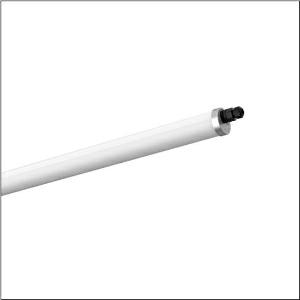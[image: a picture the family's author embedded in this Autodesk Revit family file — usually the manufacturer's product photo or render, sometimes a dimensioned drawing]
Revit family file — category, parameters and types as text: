
# Revit family: monsun_r__31_tube_51ft10dn4a0a_ff33
name_source: partatom
category: Lighting Fixtures
units: mm (PartAtom-declared; Revit-internal decimal feet)

## family parameters
Cut with Voids When Loaded = No
Host = Face
Light Source = No
Part Type = Normal
Room Calculation Point = No
Round Connector Dimension = Use Diameter
Shared = No

## types (1)
- Monsun® 31 Tube (1 x LED, 10000 lm, 58 W, 4000K)
    Apparent Load = 58 VA
    CIE Flux Codes = 42 71 90 91 100
    Color Rendering = 80
    Color Temperature = 4000K
    Default Elevation = 1800 mm
    Description = Monsun® 31 Tube, tubular luminaire, primary optical cover: diffuser, of PMMA, light emission: direct distribution, primary light characteristic: symmetric, installation type: suspended mounting, surface-mounted, LED, rated luminous flux: 10.000lm, luminous efficacy: 160lm/W, light colour: 840, colour temperature: 4000K, with with 1 terminal, 5-pole, max. 2.5mm², through-wiring: 5x 1.5mm², mains connection: 220..240V, AC, 50/60Hz, rated input power: 58W, housing, cylindrical, of PMMA, semi-transparent, matt white, with luminaire and ceiling fastening, V4A, mounting with brackets of stainless steel, length: 1.570mm, diameter: 75mm, end cap, of stainless steel (V4A), protection rating (complete): IP67/IP69K, insulation class (complete): insulation class I (protective earthing), certification: CE, UKCA, impact resistance: IK07, permissible operating ambient temperature: -20..+40°C, corresponds to IFS (International Featured Standards) requirements for safety and quality in the food industry, usage in unprotected outdoor area possible with horizontal mounting, contact your sales advisor before using the luminaires in applications with unclear chemical exposure, large temperature fluctuations or condensation-forming humidity, packaging unit: 1 piece
    Height = 83 mm
    Lamp = 1 x LED
    Lamp Light Flux = 10000 lm
    Lamp Power = 58 W
    Lamp count = 1
    Length = 1570 mm
    Luminous efficacy = 172 lm/W
    Manufacturer = Siteco
    ModVariant = No
    Model = 51FT10DN4A0A
    Mounting Place = Ceiling
    Mounting Type = Pendant
    Number of Poles = 1
    OnlyDefault = Yes
    Power Factor = 1
    Product Name = Monsun® 31 Tube
    Product group = tubular luminaire
    ProductGroupID = 906
    Protection Class = Protection class I
    RLX_Detail_Level = 1
    RLX_Emergency_Light_Flux = 0 lm
    RLX_Emergency_Type = 0
    RLX_Emergency_Type_DB = No
    RlxData = <blob elided: 25337 chars, md5=0c5fdd47>
    Socket = socket
    Standby Power = 0 W
    System Light Flux = 10000 lm
    System Power = 58 W
    Type Comments = Product without accessories
    Type Image = l_1228461.jpg
    URL = http://relux.com
    VarID = ---
    Voltage = 0 V
    Weight = 0.00 kg
    Width = 75 mm

## geometry (parser evidence)
native form markers: Blend x4, Sweep x14
no freeform markers — native parametric forms only
